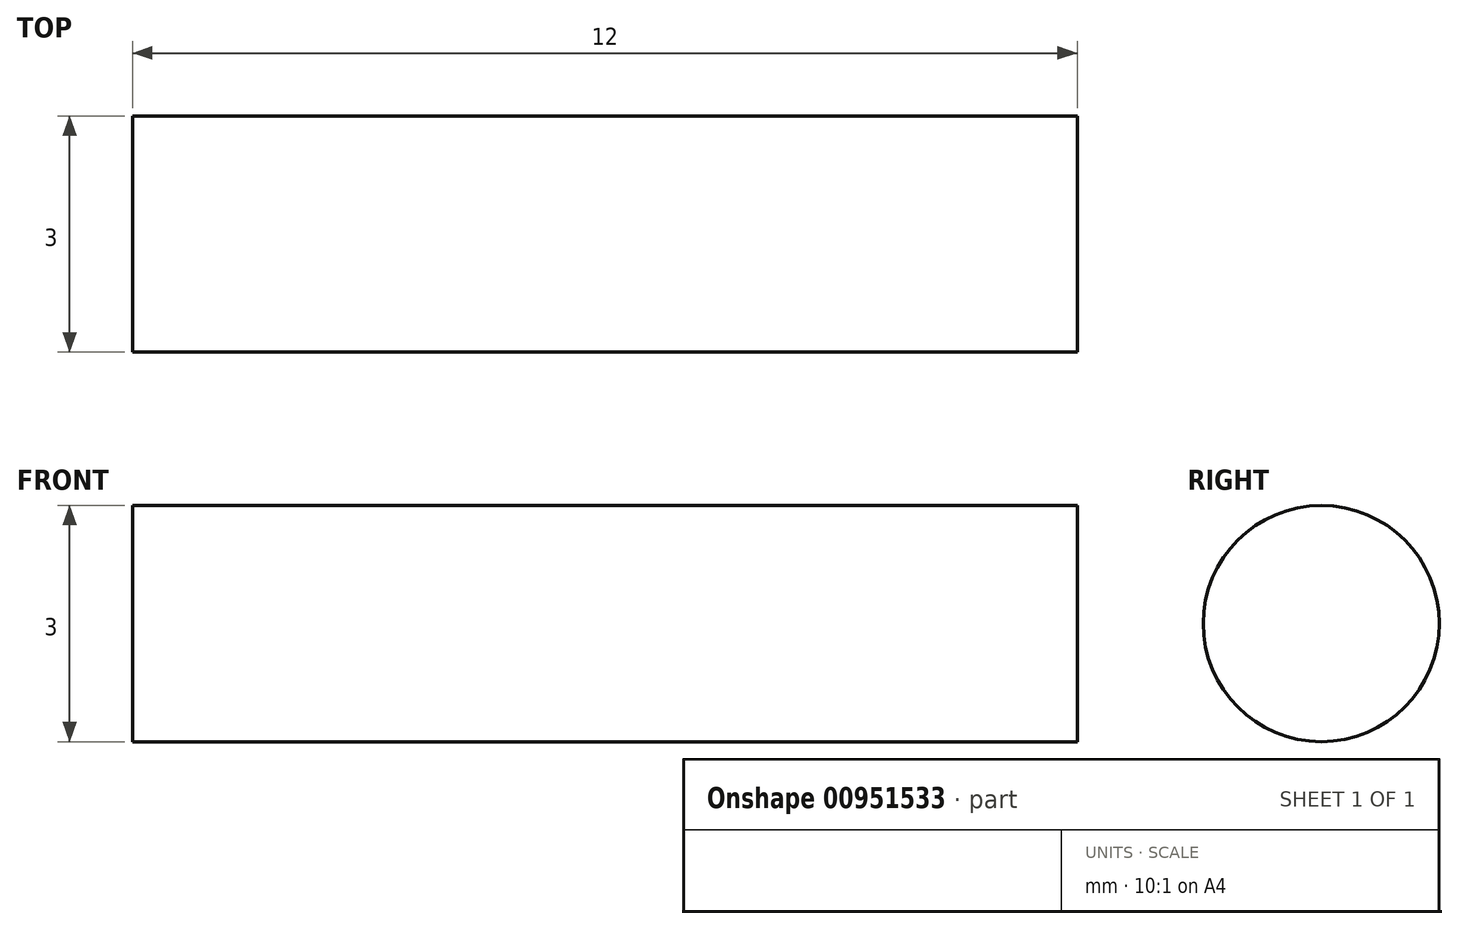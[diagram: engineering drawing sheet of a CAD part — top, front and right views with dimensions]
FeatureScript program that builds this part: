
annotation { "Feature Type Name" : "Feature", "Feature Type Description" : "" }
export const myFeature = defineFeature(function(context is Context, id is Id, definition is map)
    precondition{}
    {
        {
            var Q0;
            Q0=qCreatedBy(makeId("Right.planeOp"),FACE);
            var sketch = newSketch(context, id + "F0", { "sketchPlane" : qUnion([Q0])});
            skCircle(sketch, "E0", {"center": v(0, 0) * mm, "radius": 1.5 * mm});
            skSolve(sketch);
        }
        {
            var Q0;
            Q0 = qSketchRegion(id + "F0", true);
            extrude(context, id + "F1", {"entities" : qUnion([Q0]), "depth" : 12 * mm, "offsetDistance" : 25 * mm});
        }
    });
